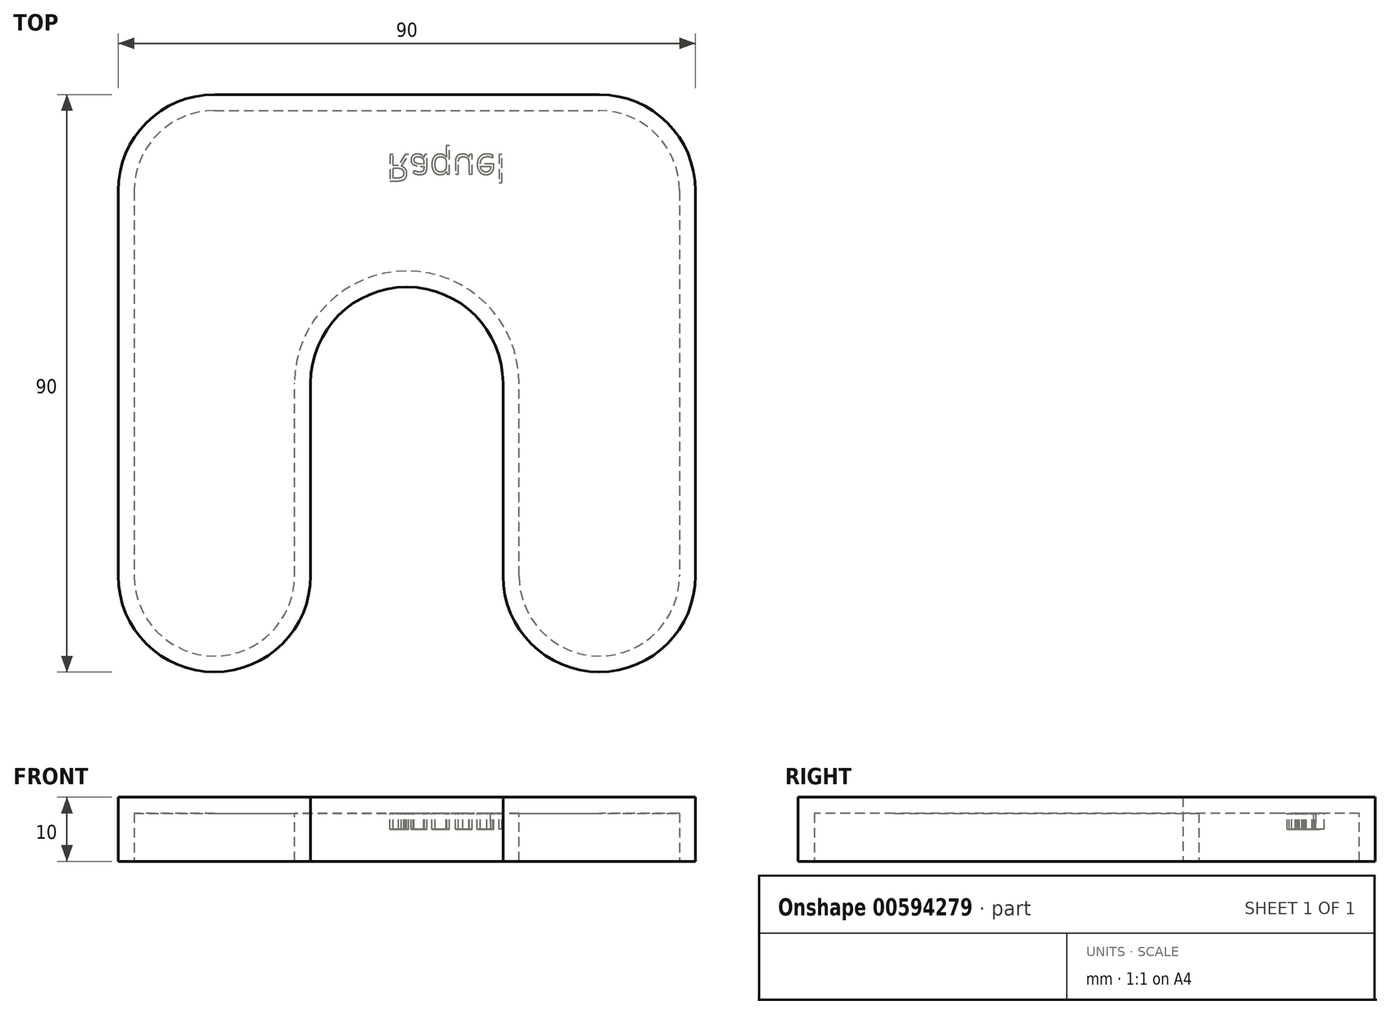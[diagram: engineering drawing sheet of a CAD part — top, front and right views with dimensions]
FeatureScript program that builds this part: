
annotation { "Feature Type Name" : "Feature", "Feature Type Description" : "" }
export const myFeature = defineFeature(function(context is Context, id is Id, definition is map)
    precondition{}
    {
        {
            var Q0;
            Q0=qCreatedBy(makeId("Top.planeOp"),FACE);
            var sketch = newSketch(context, id + "F0", { "sketchPlane" : qUnion([Q0])});
            skLineSegment(sketch, "E0.bottom", {"start": v(-28.87, 30) * mm, "end": v(31.13, 30) * mm});
            skLineSegment(sketch, "E0.left", {"start": v(-43.87, 15) * mm, "end": v(-43.87, -45) * mm});
            skLineSegment(sketch, "E0.right", {"start": v(46.13, 15) * mm, "end": v(46.13, -45) * mm});
            skLineSegment(sketch, "E1", {"start": v(-28.87, -60) * mm, "end": v(-28.87, -60) * mm});
            skLineSegment(sketch, "E2", {"start": v(31.13, -60) * mm, "end": v(31.13, -60) * mm});
            skLineSegment(sketch, "E3", {"start": v(-13.87, -45) * mm, "end": v(-13.87, -15) * mm});
            skLineSegment(sketch, "E4", {"start": v(16.13, -45) * mm, "end": v(16.13, -15) * mm});
            skLineSegment(sketch, "E5", {"start": v(1.13, 0) * mm, "end": v(1.13, 0) * mm});
            skPoint(sketch, "E6.visualSharp", {"position": v(-43.87, 30) * mm});
            skArc(sketch, "E6.filletArc", {"start": v(-28.87, 30) * mm, "mid": v(-39.48, 25.6) * mm, "end": v(-43.87, 15) * mm});
            skPoint(sketch, "E7.visualSharp", {"position": v(46.13, 30) * mm});
            skArc(sketch, "E7.filletArc", {"start": v(46.13, 15) * mm, "mid": v(41.73, 25.6) * mm, "end": v(31.13, 30) * mm});
            skPoint(sketch, "E8.visualSharp", {"position": v(-43.87, -60) * mm});
            skArc(sketch, "E8.filletArc", {"start": v(-43.87, -45) * mm, "mid": v(-39.48, -55.6) * mm, "end": v(-28.87, -60) * mm});
            skPoint(sketch, "E9.visualSharp", {"position": v(-13.87, -60) * mm});
            skArc(sketch, "E9.filletArc", {"start": v(-28.87, -60) * mm, "mid": v(-18.27, -55.6) * mm, "end": v(-13.87, -45) * mm});
            skPoint(sketch, "E10.visualSharp", {"position": v(16.13, -60) * mm});
            skArc(sketch, "E10.filletArc", {"start": v(16.13, -45) * mm, "mid": v(20.52, -55.6) * mm, "end": v(31.13, -60) * mm});
            skPoint(sketch, "E11.visualSharp", {"position": v(46.13, -60) * mm});
            skArc(sketch, "E11.filletArc", {"start": v(31.13, -60) * mm, "mid": v(41.73, -55.6) * mm, "end": v(46.13, -45) * mm});
            skPoint(sketch, "E12.visualSharp", {"position": v(-13.87, 0) * mm});
            skArc(sketch, "E12.filletArc", {"start": v(1.13, 0) * mm, "mid": v(-9.48, -4.4) * mm, "end": v(-13.87, -15) * mm});
            skPoint(sketch, "E13.visualSharp", {"position": v(16.13, 0) * mm});
            skArc(sketch, "E13.filletArc", {"start": v(16.13, -15) * mm, "mid": v(11.73, -4.4) * mm, "end": v(1.13, 0) * mm});
            skSolve(sketch);
        }
        {
            var Q0;
            Q0 = qSketchRegion(id + "F0", true);
            extrude(context, id + "F1", {"entities" : qUnion([Q0]), "depth" : 10 * mm, "offsetDistance" : 25 * mm});
        }
        {
            var Q0;
            Q0=makeQuery(id+"F1.opExtrude","CAP_FACE",FACE,{"disambiguationData":[OSD([sQuery(id+"F0.wireOp",EDGE,"E0.bottom"),sQuery(id+"F0.wireOp",EDGE,"E0.left"),sQuery(id+"F0.wireOp",EDGE,"E0.right"),sQuery(id+"F0.wireOp",EDGE,"E3"),sQuery(id+"F0.wireOp",EDGE,"E4"),sQuery(id+"F0.wireOp",EDGE,"E6.filletArc"),sQuery(id+"F0.wireOp",EDGE,"E7.filletArc"),sQuery(id+"F0.wireOp",EDGE,"E8.filletArc"),sQuery(id+"F0.wireOp",EDGE,"E9.filletArc"),sQuery(id+"F0.wireOp",EDGE,"E10.filletArc"),sQuery(id+"F0.wireOp",EDGE,"E11.filletArc"),sQuery(id+"F0.wireOp",EDGE,"E12.filletArc"),sQuery(id+"F0.wireOp",EDGE,"E13.filletArc")])],"isStart":true});
            shell(context, id + "F2", {"entities" : qUnion([Q0]), "thickness" : 2.5 * mm});
        }
        {
            var Q0;
            Q0=makeQuery(id+"F2.opShell","OFFSET_FACE",FACE,{"disambiguationData":[OSD([sQuery(id+"F0.wireOp",EDGE,"E0.bottom"),sQuery(id+"F0.wireOp",EDGE,"E0.left"),sQuery(id+"F0.wireOp",EDGE,"E0.right"),sQuery(id+"F0.wireOp",EDGE,"E3"),sQuery(id+"F0.wireOp",EDGE,"E4"),sQuery(id+"F0.wireOp",EDGE,"E6.filletArc"),sQuery(id+"F0.wireOp",EDGE,"E7.filletArc"),sQuery(id+"F0.wireOp",EDGE,"E8.filletArc"),sQuery(id+"F0.wireOp",EDGE,"E9.filletArc"),sQuery(id+"F0.wireOp",EDGE,"E10.filletArc"),sQuery(id+"F0.wireOp",EDGE,"E11.filletArc"),sQuery(id+"F0.wireOp",EDGE,"E12.filletArc"),sQuery(id+"F0.wireOp",EDGE,"E13.filletArc")])]});
            var sketch = newSketch(context, id + "F3", { "sketchPlane" : qUnion([Q0])});
            skText(sketch, "E14", { "text": "Raquel", "fontName": "OpenSans-Regular.ttf"});
            const initialGuessF3  = {"E14": [-0.00205, -0.02066, 1, 0, 0.00415]};
            skSetInitialGuess(sketch, initialGuessF3);
            skSolve(sketch);
        }
        {
            var Q0;
            Q0 = qSketchRegion(id + "F3", true);
            extrude(context, id + "F4", {"entities" : qUnion([Q0]), "operationType" : NewBodyOperationType.ADD, "depth" : 2.5 * mm, "offsetDistance" : 25 * mm});
        }
    });
